# Revit family: Wiring_Devices<unrecoverable-encoding: 3 bytes ef80ba>_Concrete_Floor_Boxes<unrecoverable-encoding: 3 bytes ef80ba>_Leviton_FBC1F-B-N
name_source: partatom
category: Electrical Fixtures
units: mm (PartAtom-declared; Revit-internal decimal feet)

## family parameters
Always vertical = Yes
Classification Number = 23.80.00.00
Cut with Voids When Loaded = No
Maintain Annotation Orientation = No
Part Type = Normal
Room Calculation Point = No
Round Connector Dimension = Use Diameter
Shared = No
Work Plane-Based = No

## types (2) — shared parameters
Floor_box_length = 7.84 "
Floor_box_width = 6.51 "
Manufacturer = Leviton Mfg. Co., Inc.
Manufacturer Fax = 631-812-6252
Manufacturer Website = http://www.leviton.com
Model = FBC1X-B
Product Data = https://www.arcat.com
Sales Information = http://www.leviton.com
zero-valued in all types: Default Elevation, Expected Lifespan (Years), Maintenance Schedule (Months), Warranty Duration (Years)

## per-type parameters (varying)
| type | Finish Material |
| FBC1F-B | Metal - Leviton - Brass |
| FBC1F-N | Metal - Leviton - Nickel |

## geometry (parser evidence)
native form markers: Blend x12, Sweep x6
no freeform markers — native parametric forms only
